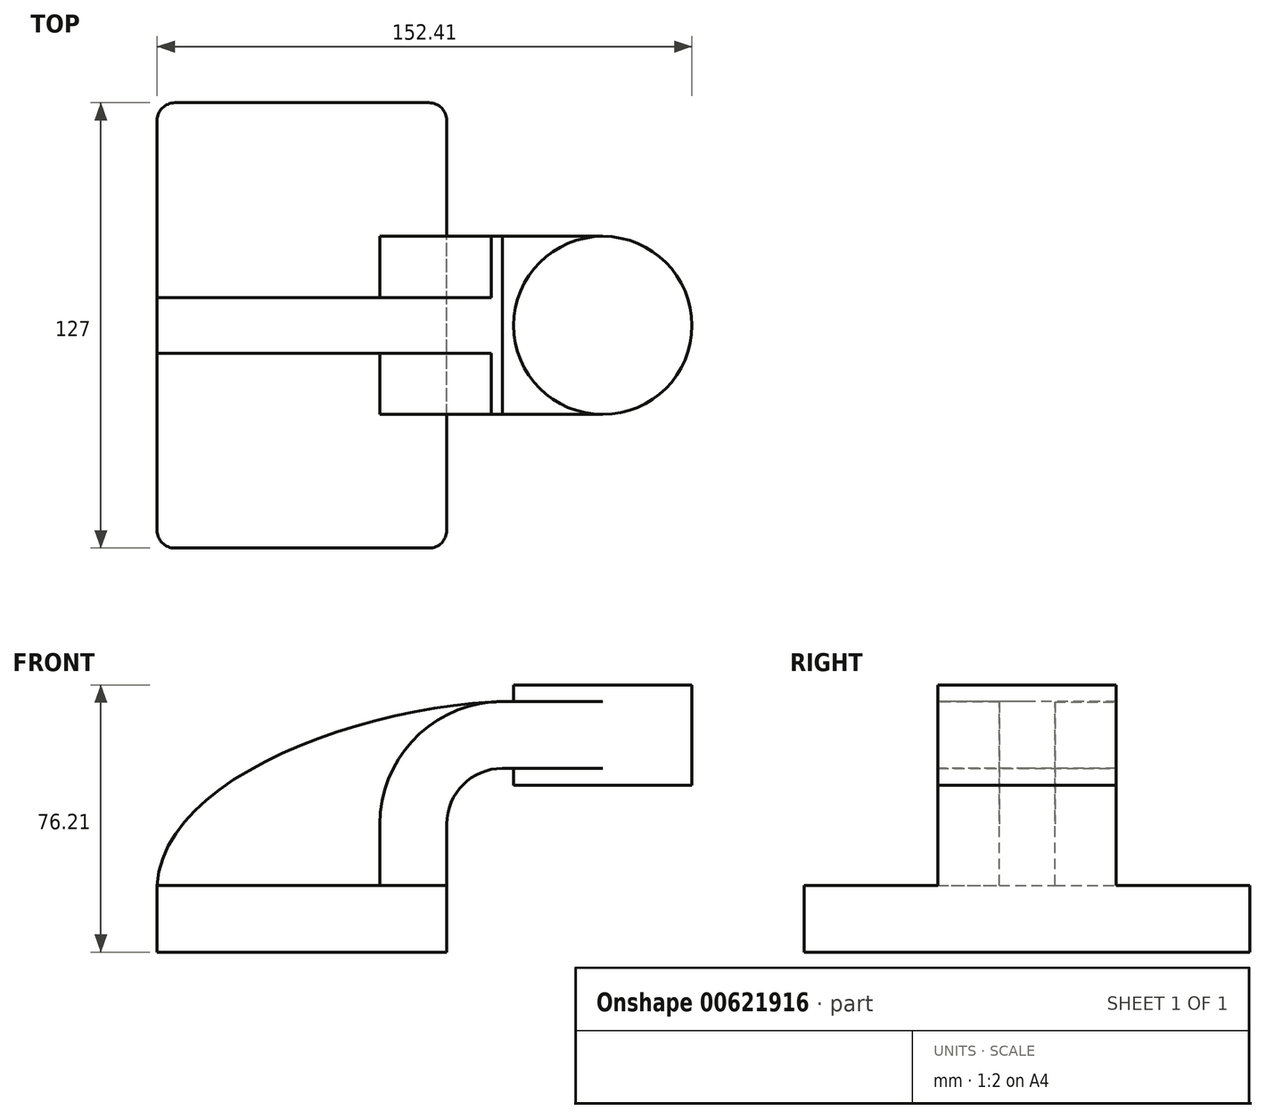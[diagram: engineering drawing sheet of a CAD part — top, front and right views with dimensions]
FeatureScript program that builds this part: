
annotation { "Feature Type Name" : "Feature", "Feature Type Description" : "" }
export const myFeature = defineFeature(function(context is Context, id is Id, definition is map)
    precondition{}
    {
        {
            var Q0;
            Q0=qCreatedBy(makeId("Front.planeOp"),FACE);
            var sketch = newSketch(context, id + "F0", { "sketchPlane" : qUnion([Q0])});
            skLineSegment(sketch, "E0.rect.bottom", {"start": v(-41.28, 9.52) * mm, "end": v(41.28, 9.52) * mm});
            skLineSegment(sketch, "E0.rect.top", {"start": v(-41.28, -9.52) * mm, "end": v(41.28, -9.52) * mm});
            skLineSegment(sketch, "E0.rect.left", {"start": v(-41.28, 9.52) * mm, "end": v(-41.28, -9.52) * mm});
            skLineSegment(sketch, "E0.rect.right", {"start": v(41.28, 9.52) * mm, "end": v(41.28, -9.52) * mm});
            skPoint(sketch, "E0.rect.middle", {"position": v(0, 0) * mm});
            skLineSegment(sketch, "E1", {"start": v(41.28, 9.52) * mm, "end": v(41.28, 27) * mm});
            skArc(sketch, "E2", {"start": v(41.28, 27) * mm, "mid": v(45.92, 38.23) * mm, "end": v(57.15, 42.88) * mm});
            skLineSegment(sketch, "E3", {"start": v(57.15, 42.88) * mm, "end": v(85.72, 42.88) * mm});
            skLineSegment(sketch, "E4.rect.bottom", {"start": v(60.32, 38.1) * mm, "end": v(111.12, 38.1) * mm});
            skLineSegment(sketch, "E4.rect.top", {"start": v(60.32, 66.68) * mm, "end": v(111.12, 66.68) * mm});
            skLineSegment(sketch, "E4.rect.left", {"start": v(60.32, 38.1) * mm, "end": v(60.32, 66.68) * mm});
            skLineSegment(sketch, "E4.rect.right", {"start": v(111.13, 38.1) * mm, "end": v(111.12, 66.68) * mm});
            skPoint(sketch, "E4.rect.middle", {"position": v(85.72, 52.39) * mm});
            skLineSegment(sketch, "E5.0", {"start": v(57.15, 61.93) * mm, "end": v(85.72, 61.93) * mm});
            skArc(sketch, "E5.1", {"start": v(22.23, 27) * mm, "mid": v(32.45, 51.7) * mm, "end": v(57.15, 61.93) * mm});
            skLineSegment(sketch, "E5.2", {"start": v(22.23, 9.52) * mm, "end": v(22.23, 27) * mm});
            skLineSegment(sketch, "E6", {"start": v(85.72, 38.1) * mm, "end": v(85.72, 66.68) * mm});
            skFitSpline(sketch, "E7", {"points": [v(-41.28, 9.52) * mm, v(57.15, 61.93) * mm], "startDerivative": vector(5.2, 92.34) * mm, "endDerivative": vector(120.92, 4.22) * mm});
            skPoint(sketch, "E8", {"position": v(85.72, 66.68) * mm});
            skPoint(sketch, "E9", {"position": v(-151.82, 708.46) * mm});
            skLineSegment(sketch, "E10", {"start": v(85.72, 66.68) * mm, "end": v(85.72, 73.49) * mm});
            skLineSegment(sketch, "E11", {"start": v(85.72, 73.49) * mm, "end": v(85.72, 33.93) * mm});
            skSolve(sketch);
        }
        {
            var Q0;
            Q0=makeQuery(id+"F0.imprint","IMPRINT",FACE,{"disambiguationData":[TD([[makeQuery(id+"F0.imprint","IMPRINT",EDGE,{"derivedFrom":sQuery(id+"F0.wireOp",EDGE,"E0.rect.top")}),1.0]])]});
            extrude(context, id + "F1", {"entities" : qUnion([Q0]), "endBound" : BoundingType.SYMMETRIC, "depth" : 127 * mm});
        }
        {
            var Q0;
            {var subQ9=sQuery(id+"F0.wireOp",EDGE,"E1");Q0=makeQuery(id+"F0.imprint","IMPRINT",FACE,{"disambiguationData":[TD([[makeQuery(id+"F0.imprint","IMPRINT",EDGE,{"derivedFrom":subQ9}),1.0]])]});}
            var Q1;
            {var subQ0=sQuery(id+"F0.wireOp",EDGE,"E6");var subQ1=sQuery(id+"F0.wireOp",EDGE,"E3");var subQ2=makeQuery(id+"F0.imprint","INTERSECT",VERTEX,{"derivedFrom":[subQ1,subQ0]});Q1=makeQuery(id+"F0.imprint","IMPRINT",FACE,{"disambiguationData":[TD([[makeQuery(id+"F0.imprint","IMPRINT",EDGE,{"disambiguationData":[TD([[subQ2,1.0]])],"derivedFrom":subQ1}),1.0]])]});}
            extrude(context, id + "F2", {"entities" : qUnion([Q0, Q1]), "operationType" : NewBodyOperationType.ADD, "endBound" : BoundingType.SYMMETRIC, "depth" : 50.8 * mm});
        }
        {
            var Q0;
            {var subQ3=sQuery(id+"F0.wireOp",EDGE,"E5.2");Q0=makeQuery(id+"F0.imprint","IMPRINT",FACE,{"disambiguationData":[TD([[makeQuery(id+"F0.imprint","IMPRINT",EDGE,{"derivedFrom":subQ3}),1.0]])]});}
            extrude(context, id + "F3", {"entities" : qUnion([Q0]), "operationType" : NewBodyOperationType.ADD, "endBound" : BoundingType.SYMMETRIC, "depth" : 15.88 * mm});
        }
        {
            var Q0;
            {var subQ5=sQuery(id+"F0.wireOp",EDGE,"E4.rect.right");Q0=makeQuery(id+"F0.imprint","IMPRINT",FACE,{"disambiguationData":[TD([[makeQuery(id+"F0.imprint","IMPRINT",EDGE,{"derivedFrom":subQ5}),1.0]])]});}
            var Q1;
            Q1=sQuery(id+"F0.wireOp",EDGE,"E6");
            revolve(context, id + "F4", {"operationType" : NewBodyOperationType.ADD, "entities" : qUnion([Q0]), "axis" : qUnion([Q1]), "revolveType" : RevolveType.FULL});
        }
        {
            var Q0;
            Q0=makeQuery(id+"F1.opExtrude","CAP_EDGE",EDGE,{"disambiguationData":[OSD([sQuery(id+"F0.wireOp",EDGE,"E0.rect.right")])],"isStart":false});
            var Q1;
            Q1=makeQuery(id+"F1.opExtrude","CAP_EDGE",EDGE,{"disambiguationData":[OSD([sQuery(id+"F0.wireOp",EDGE,"E0.rect.left")])],"isStart":false});
            var Q2;
            Q2=makeQuery(id+"F1.opExtrude","CAP_EDGE",EDGE,{"disambiguationData":[OSD([sQuery(id+"F0.wireOp",EDGE,"E0.rect.right")])],"isStart":true});
            var Q3;
            Q3=makeQuery(id+"F1.opExtrude","CAP_EDGE",EDGE,{"disambiguationData":[OSD([sQuery(id+"F0.wireOp",EDGE,"E0.rect.left")])],"isStart":true});
            fillet(context, id + "F5", {"entities" : qUnion([Q0, Q1, Q2, Q3]), "radius" : 5.08 * mm, "tangentPropagation" : true, "allowEdgeOverflow" : false});
        }
    });
